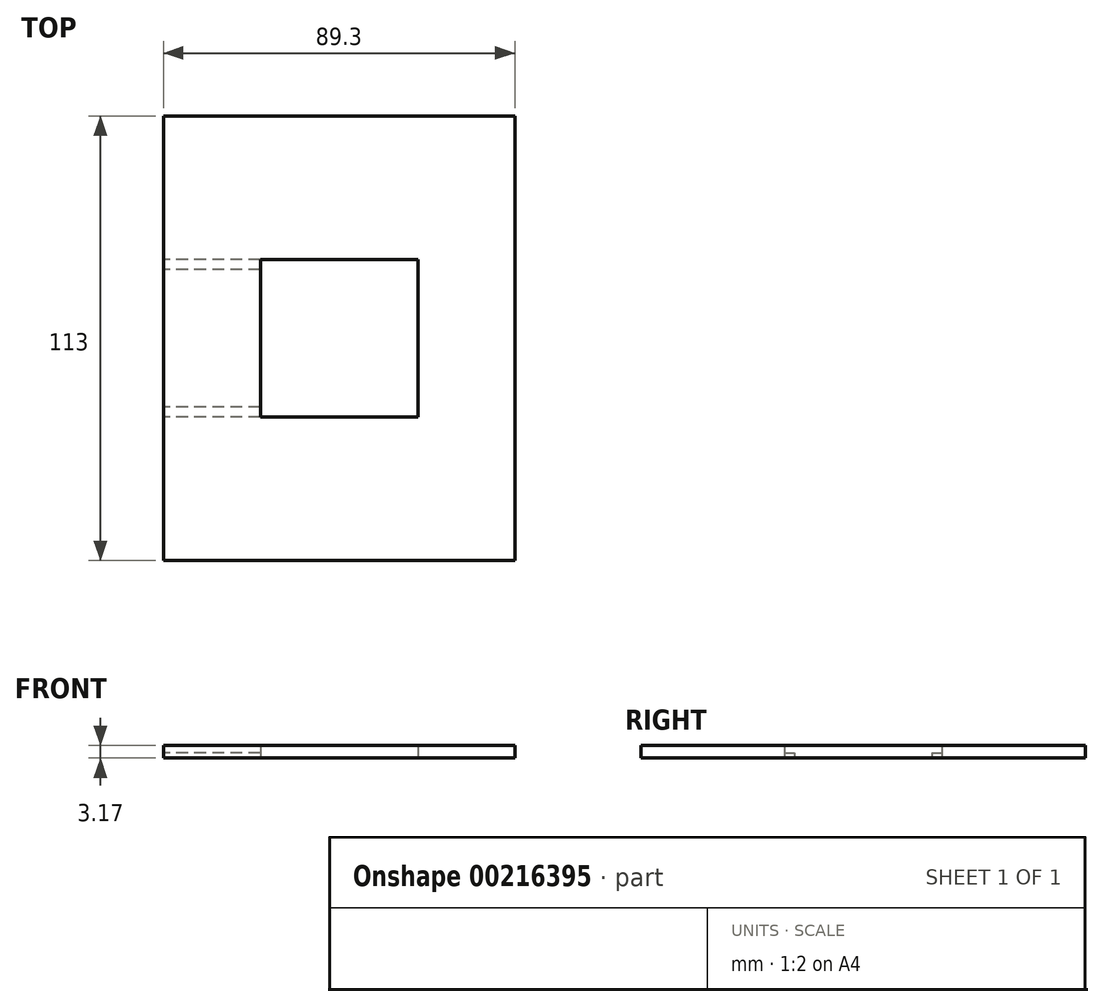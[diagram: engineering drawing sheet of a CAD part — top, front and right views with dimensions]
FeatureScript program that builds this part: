
annotation { "Feature Type Name" : "Feature", "Feature Type Description" : "" }
export const myFeature = defineFeature(function(context is Context, id is Id, definition is map)
    precondition{}
    {
        {
            var Q0;
            Q0=qCreatedBy(makeId("Top.planeOp"),FACE);
            var sketch = newSketch(context, id + "F0", { "sketchPlane" : qUnion([Q0])});
            skLineSegment(sketch, "E0.bottom", {"start": v(-44.65, -56.5) * mm, "end": v(44.65, -56.5) * mm});
            skLineSegment(sketch, "E0.top", {"start": v(-44.65, 56.5) * mm, "end": v(44.65, 56.5) * mm});
            skLineSegment(sketch, "E0.left", {"start": v(-44.65, -56.5) * mm, "end": v(-44.65, 56.5) * mm});
            skLineSegment(sketch, "E0.right", {"start": v(44.65, -56.5) * mm, "end": v(44.65, 56.5) * mm});
            skPoint(sketch, "E0.middle", {"position": v(0, 0) * mm});
            skLineSegment(sketch, "E1.bottom", {"start": v(-20, -20) * mm, "end": v(20, -20) * mm});
            skLineSegment(sketch, "E1.top", {"start": v(-20, 20) * mm, "end": v(20, 20) * mm});
            skLineSegment(sketch, "E1.left", {"start": v(-20, -20) * mm, "end": v(-20, 20) * mm});
            skLineSegment(sketch, "E1.right", {"start": v(20, -20) * mm, "end": v(20, 20) * mm});
            skLineSegment(sketch, "E2.right", {"start": v(-44.65, -20) * mm, "end": v(-44.65, -17.46) * mm});
            skLineSegment(sketch, "E3.right", {"start": v(-44.65, 20) * mm, "end": v(-44.65, 17.46) * mm});
            skSolve(sketch);
        }
        {
            var Q0;
            {var subQ3=sQuery(id+"F0.wireOp",EDGE,"E0.bottom");Q0=makeQuery(id+"F0.imprint","IMPRINT",FACE,{"disambiguationData":[TD([[makeQuery(id+"F0.imprint","IMPRINT",EDGE,{"derivedFrom":subQ3}),1.0]])]});}
            extrude(context, id + "F1", {"entities" : qUnion([Q0]), "depth" : 3.17 * mm});
        }
        {
            var Q0;
            Q0=makeQuery(id+"F1.opExtrude","CAP_FACE",FACE,{"disambiguationData":[OSD([sQuery(id+"F0.wireOp",EDGE,"E0.bottom"),sQuery(id+"F0.wireOp",EDGE,"E0.top"),sQuery(id+"F0.wireOp",EDGE,"E0.left"),sQuery(id+"F0.wireOp",EDGE,"E0.right"),sQuery(id+"F0.wireOp",EDGE,"E1.bottom"),sQuery(id+"F0.wireOp",EDGE,"E1.top"),sQuery(id+"F0.wireOp",EDGE,"E1.left"),sQuery(id+"F0.wireOp",EDGE,"E1.right"),sQuery(id+"F0.wireOp",EDGE,"E2.right"),sQuery(id+"F0.wireOp",EDGE,"E3.right")])],"isStart":true});
            var sketch = newSketch(context, id + "F2", { "sketchPlane" : qUnion([Q0])});
            skLineSegment(sketch, "E4.bottom", {"start": v(-20, 20) * mm, "end": v(-44.65, 20) * mm});
            skLineSegment(sketch, "E4.top", {"start": v(-20, 17.46) * mm, "end": v(-44.65, 17.46) * mm});
            skLineSegment(sketch, "E4.left", {"start": v(-20, 20) * mm, "end": v(-20, 17.46) * mm});
            skLineSegment(sketch, "E4.right", {"start": v(-44.65, 20) * mm, "end": v(-44.65, 17.46) * mm});
            skLineSegment(sketch, "E5.bottom", {"start": v(-20, -20) * mm, "end": v(-44.65, -20) * mm});
            skLineSegment(sketch, "E5.top", {"start": v(-20, -17.46) * mm, "end": v(-44.65, -17.46) * mm});
            skLineSegment(sketch, "E5.left", {"start": v(-20, -20) * mm, "end": v(-20, -17.46) * mm});
            skLineSegment(sketch, "E5.right", {"start": v(-44.65, -20) * mm, "end": v(-44.65, -17.46) * mm});
            skSolve(sketch);
        }
        {
            var Q0;
            Q0 = qSketchRegion(id + "F2", true);
            extrude(context, id + "F3", {"entities" : qUnion([Q0]), "operationType" : NewBodyOperationType.REMOVE, "oppositeDirection" : true, "depth" : 1.27 * mm});
        }
    });
